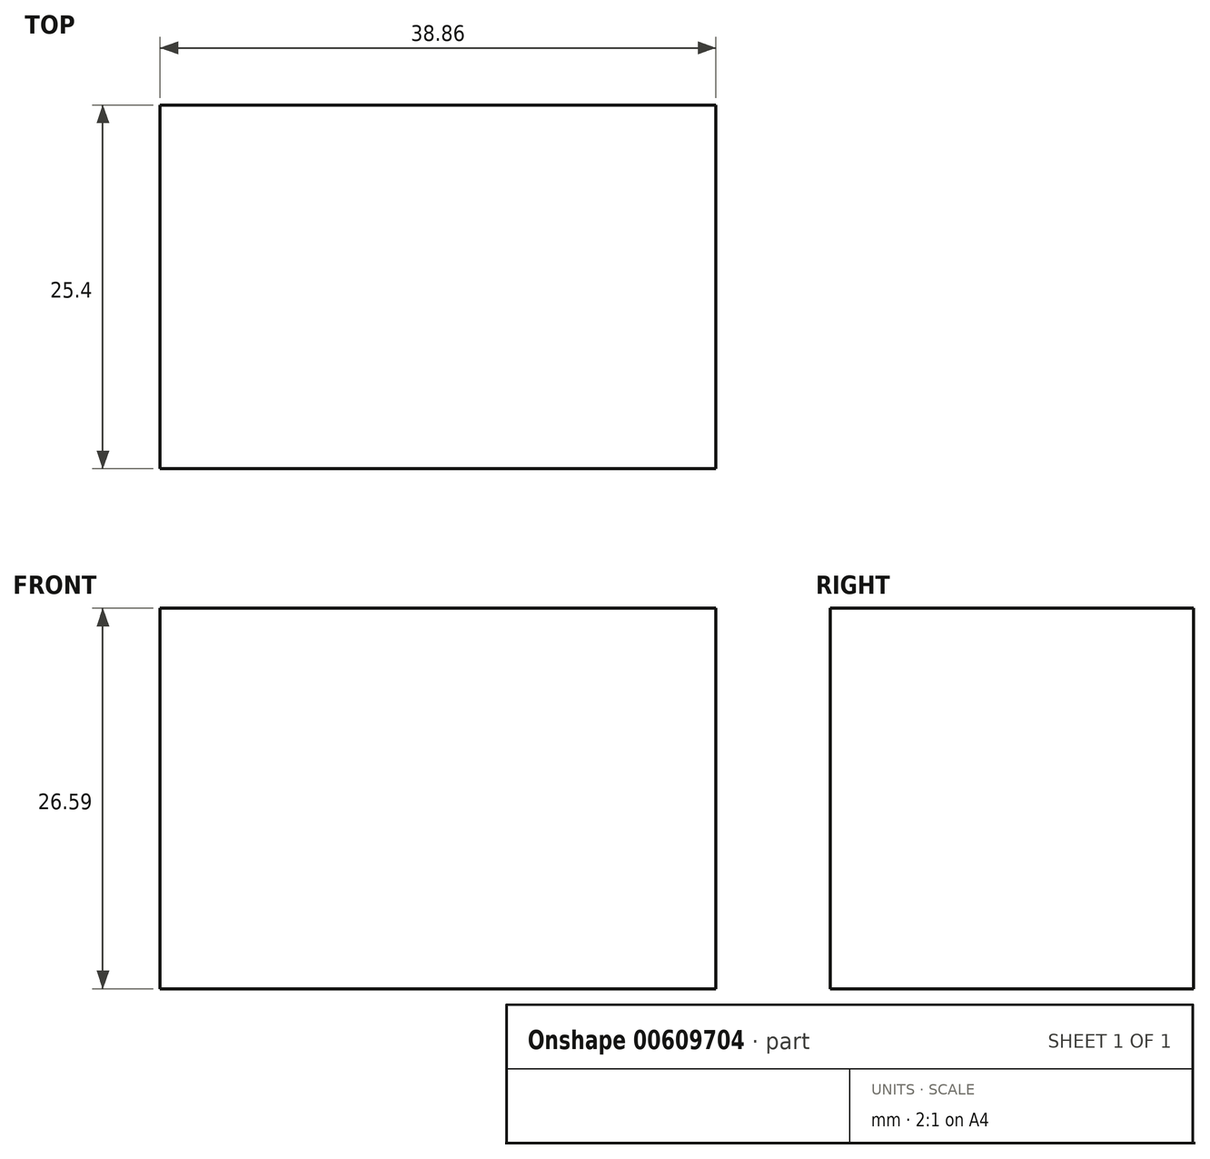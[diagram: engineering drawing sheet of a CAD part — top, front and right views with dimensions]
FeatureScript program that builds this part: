
annotation { "Feature Type Name" : "Feature", "Feature Type Description" : "" }
export const myFeature = defineFeature(function(context is Context, id is Id, definition is map)
    precondition{}
    {
        {
            var Q0;
            Q0=qCreatedBy(makeId("Front.planeOp"),FACE);
            var sketch = newSketch(context, id + "F0", { "sketchPlane" : qUnion([Q0])});
            skLineSegment(sketch, "E0.bottom", {"start": v(-95.32, 54.41) * mm, "end": v(-56.46, 54.41) * mm});
            skLineSegment(sketch, "E0.top", {"start": v(-95.32, 27.82) * mm, "end": v(-56.46, 27.82) * mm});
            skLineSegment(sketch, "E0.left", {"start": v(-95.32, 54.41) * mm, "end": v(-95.32, 27.82) * mm});
            skLineSegment(sketch, "E0.right", {"start": v(-56.46, 54.41) * mm, "end": v(-56.46, 27.82) * mm});
            skSolve(sketch);
        }
        {
            var Q0;
            Q0 = qSketchRegion(id + "F0", true);
            extrude(context, id + "F1", {"entities" : qUnion([Q0]), "depth" : 25.4 * mm, "offsetDistance" : 25.4 * mm});
        }
    });
